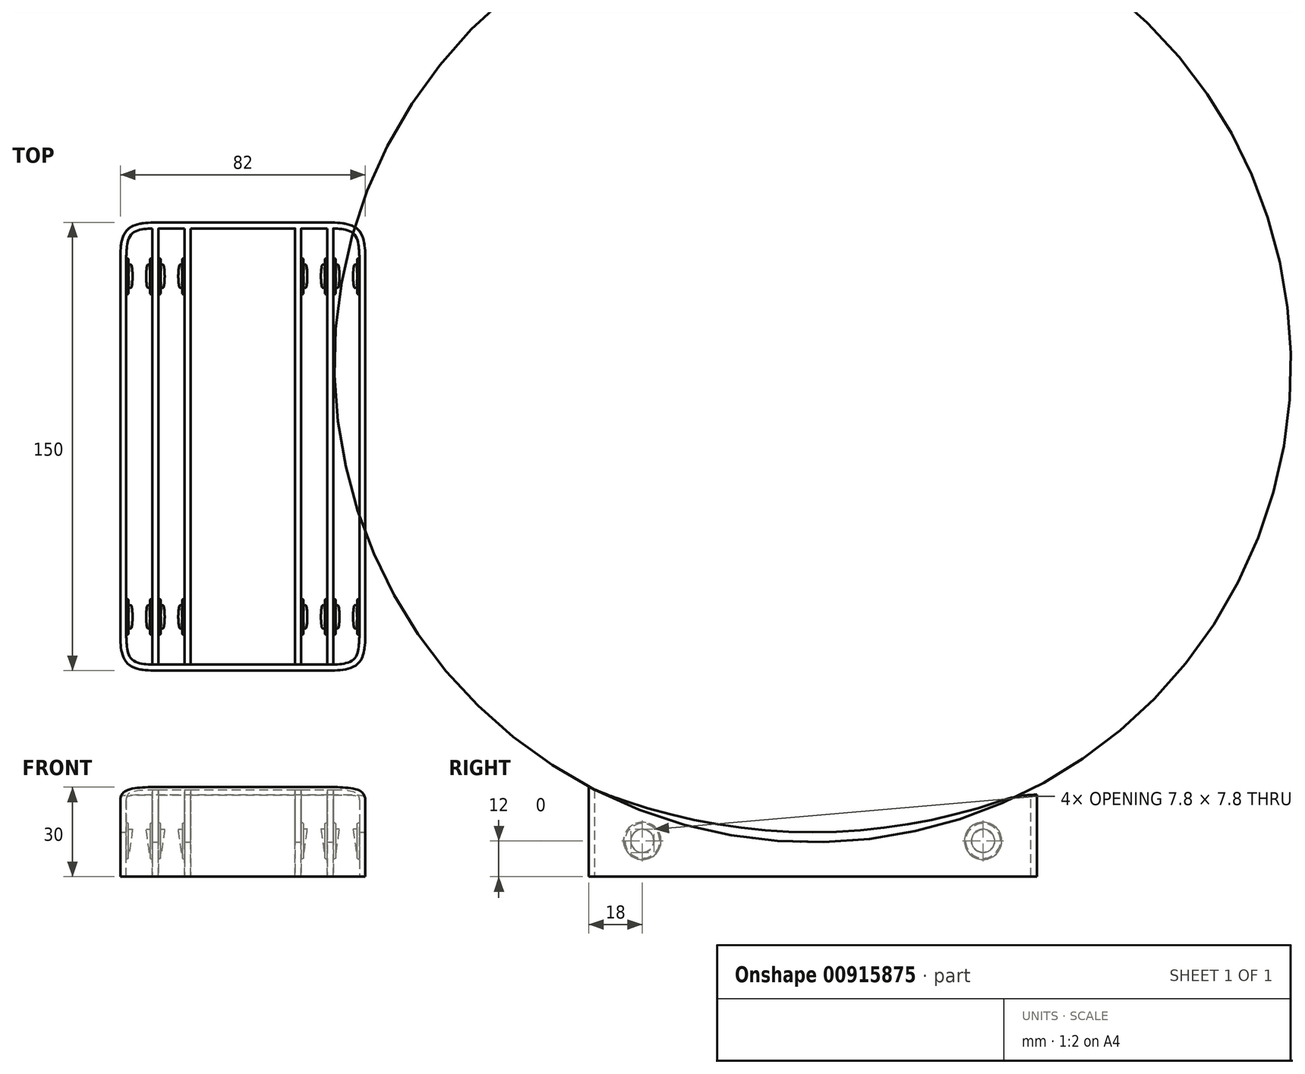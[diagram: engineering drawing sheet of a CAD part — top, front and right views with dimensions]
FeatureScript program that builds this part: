
annotation { "Feature Type Name" : "Feature", "Feature Type Description" : "" }
export const myFeature = defineFeature(function(context is Context, id is Id, definition is map)
    precondition{}
    {
        {
            var Q0;
            Q0=qCreatedBy(makeId("Top.planeOp"),FACE);
            var sketch = newSketch(context, id + "F0", { "sketchPlane" : qUnion([Q0])});
            skLineSegment(sketch, "E0.bottom", {"start": v(-41, 75) * mm, "end": v(41, 75) * mm});
            skLineSegment(sketch, "E0.top", {"start": v(-41, -75) * mm, "end": v(41, -75) * mm});
            skLineSegment(sketch, "E0.left", {"start": v(-41, 75) * mm, "end": v(-41, -75) * mm});
            skLineSegment(sketch, "E0.right", {"start": v(41, 75) * mm, "end": v(41, -75) * mm});
            skPoint(sketch, "E0.middle", {"position": v(0, 0) * mm});
            skSolve(sketch);
        }
        {
            var Q0;
            Q0=qSketchRegion(id+"F0",true);
            extrude(context, id + "F1", {"entities" : qUnion([Q0]), "depth" : 30 * mm, "offsetDistance" : 25 * mm});
        }
        {
            var Q0;
            Q0=makeQuery(id+"F1.opExtrude","SWEPT_EDGE",EDGE,{"disambiguationData":[OSD([sQuery(id+"F0.wireOp",EDGE,"E0.top"),sQuery(id+"F0.wireOp",EDGE,"E0.right")])]});
            var Q1;
            Q1=makeQuery(id+"F1.opExtrude","SWEPT_EDGE",EDGE,{"disambiguationData":[OSD([sQuery(id+"F0.wireOp",EDGE,"E0.top"),sQuery(id+"F0.wireOp",EDGE,"E0.left")])]});
            var Q2;
            Q2=makeQuery(id+"F1.opExtrude","SWEPT_EDGE",EDGE,{"disambiguationData":[OSD([sQuery(id+"F0.wireOp",EDGE,"E0.bottom"),sQuery(id+"F0.wireOp",EDGE,"E0.right")])]});
            var Q3;
            Q3=makeQuery(id+"F1.opExtrude","SWEPT_EDGE",EDGE,{"disambiguationData":[OSD([sQuery(id+"F0.wireOp",EDGE,"E0.bottom"),sQuery(id+"F0.wireOp",EDGE,"E0.left")])]});
            fillet(context, id + "F2", {"entities" : qUnion([Q0, Q1, Q2, Q3]), "radius" : 12 * mm, "tangentPropagation" : true, "rho" : .6, "crossSection" : FilletCrossSection.CONIC, "allowEdgeOverflow" : false});
        }
        {
            var Q0;
            Q0=makeQuery(id+"F20.boolean.opBoolean","COPY",FACE,{"derivedFrom":makeQuery(id+"F20.opExtrude","SWEPT_FACE",FACE,{"disambiguationData":[OSD([sQuery(id+"F19.wireOp",EDGE,"E26")])]})});
            var Q1;
            Q1=makeQuery(id+"F1.opExtrude","CAP_FACE",FACE,{"disambiguationData":[OSD([sQuery(id+"F0.wireOp",EDGE,"E0.bottom"),sQuery(id+"F0.wireOp",EDGE,"E0.top"),sQuery(id+"F0.wireOp",EDGE,"E0.left"),sQuery(id+"F0.wireOp",EDGE,"E0.right")])],"isStart":true});
            var Q2;
            Q2=makeQuery(id+"F1.opExtrude","CAP_FACE",FACE,{"disambiguationData":[OSD([sQuery(id+"F0.wireOp",EDGE,"E0.bottom"),sQuery(id+"F0.wireOp",EDGE,"E0.top"),sQuery(id+"F0.wireOp",EDGE,"E0.left"),sQuery(id+"F0.wireOp",EDGE,"E0.right")])],"isStart":false});
            shell(context, id + "F3", {"entities" : qUnion([Q0, Q1, Q2]), "thickness" : 2 * mm});
        }
        {
            var Q0;
            Q0=makeQuery(id+"F3.opShell","OFFSET_FACE",FACE,{"disambiguationData":[OSD([sQuery(id+"F0.wireOp",EDGE,"E0.bottom")])]});
            cPlane(context, id + "F4", {"entities" : qUnion([Q0]), "cplaneType" : CPlaneType.OFFSET, "offset" : 16 * mm, "width" : 150 * mm, "height" : 150 * mm});
        }
        {
            var Q0;
            Q0=makeQuery(id+"F3.opShell","OFFSET_FACE",FACE,{"disambiguationData":[OSD([sQuery(id+"F0.wireOp",EDGE,"E0.bottom")])]});
            var sketch = newSketch(context, id + "F5", { "sketchPlane" : qUnion([Q0])});
            skLineSegment(sketch, "E1", {"start": v(-30.25, 0) * mm, "end": v(-30.25, 30) * mm});
            skLineSegment(sketch, "E2", {"start": v(-28.25, 30) * mm, "end": v(-30.25, 30) * mm});
            skLineSegment(sketch, "E3", {"start": v(-28.25, 30) * mm, "end": v(-28.25, 0) * mm});
            skLineSegment(sketch, "E4", {"start": v(-28.25, 0) * mm, "end": v(-30.25, 0) * mm});
            skLineSegment(sketch, "E5.bottom", {"start": v(-19.5, 0) * mm, "end": v(-17.5, 0) * mm});
            skLineSegment(sketch, "E5.top", {"start": v(-19.5, 30) * mm, "end": v(-17.5, 30) * mm});
            skLineSegment(sketch, "E5.left", {"start": v(-19.5, 0) * mm, "end": v(-19.5, 30) * mm});
            skLineSegment(sketch, "E5.right", {"start": v(-17.5, 0) * mm, "end": v(-17.5, 30) * mm});
            skLineSegment(sketch, "E6", {"start": v(-19.5, 0) * mm, "end": v(-28.25, 0) * mm, "construction": true});
            skLineSegment(sketch, "E7", {"start": v(-30.25, 0) * mm, "end": v(-39, 0) * mm, "construction": true});
            skSolve(sketch);
        }
        {
            var Q0;
            Q0 = qSketchRegion(id + "F5", true);
            var Q1;
            Q1=makeQuery(id+"F3.opShell","OFFSET_FACE",FACE,{"disambiguationData":[OSD([sQuery(id+"F0.wireOp",EDGE,"E0.top")])]});
            extrude(context, id + "F6", {"entities" : qUnion([Q0]), "operationType" : NewBodyOperationType.ADD, "endBound" : BoundingType.UP_TO_SURFACE, "depth" : 12 * mm, "endBoundEntityFace" : qUnion([Q1]), "offsetDistance" : 25 * mm});
        }
        {
            var Q0;
            Q0=makeQuery(id+"F6.opExtrude","SWEPT_FACE",FACE,{"disambiguationData":[OSD([sQuery(id+"F5.wireOp",EDGE,"E1")])]});
            var sketch = newSketch(context, id + "F7", { "sketchPlane" : qUnion([Q0])});
            skCircle(sketch, "E8", {"center": v(-57, 12) * mm, "radius": 6.25 * mm});
            skSolve(sketch);
        }
        {
            var Q0;
            Q0=qSketchRegion(id+"F7",true);
            var Q1;
            Q1=makeQuery(id+"F6.opExtrude","SWEPT_FACE",FACE,{"disambiguationData":[OSD([sQuery(id+"F5.wireOp",EDGE,"E1")])]});
            extrude(context, id + "F8", {"entities" : qUnion([Q0]), "operationType" : NewBodyOperationType.ADD, "depth" : .75 * mm, "endBoundEntityFace" : qUnion([Q1]), "offsetDistance" : 25 * mm, "hasDraft" : true, "draftAngle" : 30 * degree, "draftPullDirection" : true, "hasSecondDirectionDraft" : true, "secondDirectionDraftAngle" : 15 * degree, "secondDirectionDraftPullDirection" : true});
        }
        {
            var Q0;
            Q0=makeQuery(id+"F3.opShell","OFFSET_FACE",FACE,{"disambiguationData":[OSD([sQuery(id+"F0.wireOp",EDGE,"E0.left")])]});
            var sketch = newSketch(context, id + "F9", { "sketchPlane" : qUnion([Q0])});
            skCircle(sketch, "E9.0", {"center": v(57, 12) * mm, "radius": 6.25 * mm});
            skSolve(sketch);
        }
        {
            var Q0;
            Q0=qSketchRegion(id+"F9",true);
            extrude(context, id + "F10", {"entities" : qUnion([Q0]), "operationType" : NewBodyOperationType.ADD, "depth" : .75 * mm, "offsetDistance" : 25 * mm, "hasDraft" : true, "draftAngle" : 30 * degree, "draftPullDirection" : true});
        }
        {
            var Q0;
            Q0=makeQuery(id+"F6.opExtrude","SWEPT_FACE",FACE,{"disambiguationData":[OSD([sQuery(id+"F5.wireOp",EDGE,"E3")])]});
            var sketch = newSketch(context, id + "F11", { "sketchPlane" : qUnion([Q0])});
            skCircle(sketch, "E10.0", {"center": v(57, 12) * mm, "radius": 6.25 * mm});
            skSolve(sketch);
        }
        {
            var Q0;
            Q0=makeQuery(id+"F6.opExtrude","SWEPT_FACE",FACE,{"disambiguationData":[OSD([sQuery(id+"F5.wireOp",EDGE,"E5.left")])]});
            var sketch = newSketch(context, id + "F12", { "sketchPlane" : qUnion([Q0])});
            skCircle(sketch, "E11.0", {"center": v(-57, 12) * mm, "radius": 6.25 * mm});
            skSolve(sketch);
        }
        {
            var Q0;
            Q0 = qSketchRegion(id + "F11", true);
            extrude(context, id + "F13", {"entities" : qUnion([Q0]), "operationType" : NewBodyOperationType.ADD, "depth" : .75 * mm, "offsetDistance" : 25 * mm, "hasDraft" : true, "draftAngle" : 30 * degree, "draftPullDirection" : true});
        }
        {
            var Q0;
            Q0 = qSketchRegion(id + "F12", true);
            var Q1;
            Q1 = qSketchRegion(id + "F15", true);
            extrude(context, id + "F14", {"entities" : qUnion([Q0, Q1]), "operationType" : NewBodyOperationType.ADD, "depth" : .75 * mm, "offsetDistance" : 25 * mm, "hasDraft" : true, "draftAngle" : 30 * degree, "draftPullDirection" : true});
        }
        {
            var Q0;
            Q0=makeQuery(id+"F8.opExtrude","CAP_FACE",FACE,{"disambiguationData":[OSD([sQuery(id+"F7.wireOp",EDGE,"E8")])],"isStart":false});
            var sketch = newSketch(context, id + "F15", { "sketchPlane" : qUnion([Q0])});
            skCircle(sketch, "E12", {"center": v(-57, 12) * mm, "radius": 3.9 * mm});
            skLineSegment(sketch, "E13", {"start": v(-57, 8.1) * mm, "end": v(-57, 15.9) * mm, "construction": true});
            skSolve(sketch);
        }
        {
            var Q0;
            Q0=qSketchRegion(id+"F15",true);
            var Q1;
            Q1=makeQuery(id+"F10.opExtrude","CAP_FACE",FACE,{"disambiguationData":[OSD([sQuery(id+"F9.wireOp",EDGE,"E9.0")])],"isStart":false});
            var Q2;
            Q2=makeQuery(id+"F14.opExtrude","CAP_FACE",FACE,{"disambiguationData":[OSD([sQuery(id+"F12.wireOp",EDGE,"E11.0")])],"isStart":false});
            extrude(context, id + "F16", {"entities" : qUnion([Q0]), "operationType" : NewBodyOperationType.ADD, "endBound" : BoundingType.UP_TO_SURFACE, "depth" : 25 * mm, "endBoundEntityFace" : qUnion([Q1]), "offsetDistance" : 25 * mm, "hasSecondDirection" : true, "secondDirectionBound" : SecondDirectionBoundingType.UP_TO_SURFACE, "secondDirectionOppositeDirection" : true, "secondDirectionDepth" : 25 * mm, "secondDirectionBoundEntityFace" : qUnion([Q2])});
        }
        {
            var Q0;
            Q0=qCreatedBy(id+"F4.planeOp",FACE);
            var sketch = newSketch(context, id + "F17", { "sketchPlane" : qUnion([Q0])});
            skLineSegment(sketch, "E14", {"start": v(-36.9, 15.9) * mm, "end": v(-38, 8.1) * mm});
            skLineSegment(sketch, "E15", {"start": v(-38, 8.1) * mm, "end": v(-31.25, 8.1) * mm});
            skLineSegment(sketch, "E16", {"start": v(-32.35, 15.9) * mm, "end": v(-31.25, 8.1) * mm});
            skLineSegment(sketch, "E17", {"start": v(-32.35, 15.9) * mm, "end": v(-36.9, 15.9) * mm});
            skLineSegment(sketch, "E18", {"start": v(-31.25, 8.1) * mm, "end": v(-31, 8.1) * mm, "construction": true});
            skLineSegment(sketch, "E19", {"start": v(-38, 8.1) * mm, "end": v(-38.25, 8.1) * mm, "construction": true});
            skLineSegment(sketch, "E20", {"start": v(-27.25, 8.1) * mm, "end": v(-26.15, 15.9) * mm});
            skLineSegment(sketch, "E21", {"start": v(-26.15, 15.9) * mm, "end": v(-21.6, 15.9) * mm});
            skLineSegment(sketch, "E22", {"start": v(-21.6, 15.9) * mm, "end": v(-20.5, 8.1) * mm});
            skLineSegment(sketch, "E23", {"start": v(-20.5, 8.1) * mm, "end": v(-27.25, 8.1) * mm});
            skLineSegment(sketch, "E24", {"start": v(-27.25, 8.1) * mm, "end": v(-27.5, 8.1) * mm, "construction": true});
            skLineSegment(sketch, "E25", {"start": v(-20.5, 8.1) * mm, "end": v(-20.25, 8.1) * mm, "construction": true});
            skSolve(sketch);
        }
        {
            var Q0;
            Q0=qSketchRegion(id+"F17",true);
            var Q1;
            Q1=makeQuery(id+"F3.opShell","OFFSET_FACE",FACE,{"disambiguationData":[OSD([sQuery(id+"F0.wireOp",EDGE,"E0.bottom"),sQuery(id+"F0.wireOp",EDGE,"E0.left")])]});
            extrude(context, id + "F18", {"entities" : qUnion([Q0]), "operationType" : NewBodyOperationType.REMOVE, "endBound" : BoundingType.SYMMETRIC, "oppositeDirection" : true, "depth" : 12 * mm, "endBoundEntityFace" : qUnion([Q1]), "offsetDistance" : 25 * mm});
        }
        {
            var Q0;
            Q0=makeQuery(id+"F1.opExtrude","SWEPT_FACE",FACE,{"disambiguationData":[OSD([sQuery(id+"F0.wireOp",EDGE,"E0.right")])]});
            var sketch = newSketch(context, id + "F19", { "sketchPlane" : qUnion([Q0])});
            skArc(sketch, "E26", {"start": v(-75, 30) * mm, "mid": v(0, 14.92) * mm, "end": v(75, 30) * mm});
            skLineSegment(sketch, "E27", {"start": v(-75, 30) * mm, "end": v(75, 30) * mm});
            skCircle(sketch, "E28", {"center": v(57, 12) * mm, "radius": 11 * mm, "construction": true});
            skArc(sketch, "E29", {"start": v(0, 2.94) * mm, "mid": v(53.33, 23.3) * mm, "end": v(79.5, 74.05) * mm, "construction": true});
            skLineSegment(sketch, "E30", {"start": v(0, 2.94) * mm, "end": v(-29.27, 2.94) * mm, "construction": true});
            skLineSegment(sketch, "E31", {"start": v(-24.7, 7.25) * mm, "end": v(0, 7.25) * mm, "construction": true});
            skPoint(sketch, "E31.endSnap0", {"position": v(0, 14.92) * mm});
            skArc(sketch, "E32", {"start": v(0, 7.25) * mm, "mid": v(58.45, 26.1) * mm, "end": v(94.85, 75.57) * mm, "construction": true});
            skSolve(sketch);
        }
        {
            var Q0;
            Q0=qSketchRegion(id+"F19",true);
            extrude(context, id + "F20", {"entities" : qUnion([Q0]), "operationType" : NewBodyOperationType.REMOVE, "endBound" : BoundingType.THROUGH_ALL, "oppositeDirection" : true, "depth" : 25 * mm, "offsetDistance" : 25 * mm});
        }
        {
            var Q0;
            Q0=qCreatedBy(makeId("Front.planeOp"),FACE);
            var sketch = newSketch(context, id + "F21", { "sketchPlane" : qUnion([Q0])});
            skLineSegment(sketch, "E33", {"start": v(0, 0) * mm, "end": v(0, 24.52) * mm, "construction": true});
            skSolve(sketch);
        }
        {
            var Q0;
            Q0=makeQuery(id+"F1.opExtrude","SWEPT_BODY",BODY,{"disambiguationData":[OSD([sQuery(id+"F0.wireOp",EDGE,"E0.bottom"),sQuery(id+"F0.wireOp",EDGE,"E0.top"),sQuery(id+"F0.wireOp",EDGE,"E0.left"),sQuery(id+"F0.wireOp",EDGE,"E0.right")])]});
            var Q1;
            Q1=sQuery(id+"F21.wireOp",EDGE,"E33");
            circularPattern(context, id + "F22", {"operationType" : NewBodyOperationType.ADD, "entities" : qUnion([Q0]), "axis" : qUnion([Q1]), "angle" : 360 * degree, "instanceCount" : 2, "equalSpace" : true});
        }
        {
            var Q0;
            Q0=makeQuery(id+"F1.opExtrude","SWEPT_BODY",BODY,{"disambiguationData":[OSD([sQuery(id+"F0.wireOp",EDGE,"E0.bottom"),sQuery(id+"F0.wireOp",EDGE,"E0.top"),sQuery(id+"F0.wireOp",EDGE,"E0.left"),sQuery(id+"F0.wireOp",EDGE,"E0.right")])]});
            var Q1;
            Q1=qCreatedBy(makeId("Right.planeOp"),FACE);
            mirror(context, id + "F23", {"operationType" : NewBodyOperationType.ADD, "entities" : qUnion([Q0]), "mirrorPlane" : qUnion([Q1])});
        }
        {
            var Q0;
            Q0=qCreatedBy(makeId("Top.planeOp"),FACE);
            var sketch = newSketch(context, id + "F24", { "sketchPlane" : qUnion([Q0])});
            skLineSegment(sketch, "E34.bottom", {"start": v(38.22, 88.74) * mm, "end": v(-49.86, 88.74) * mm});
            skLineSegment(sketch, "E34.top", {"start": v(38.22, 39.81) * mm, "end": v(-49.86, 39.81) * mm});
            skLineSegment(sketch, "E34.left", {"start": v(38.22, 88.74) * mm, "end": v(38.22, 39.81) * mm});
            skLineSegment(sketch, "E34.right", {"start": v(-49.86, 88.74) * mm, "end": v(-49.86, 39.81) * mm});
            skPoint(sketch, "E34.middle", {"position": v(-5.82, 64.28) * mm});
            skSolve(sketch);
        }
        {
            var Q0;
            Q0=makeQuery(id+"F22.opPattern","COPY",FACE,{"derivedFrom":makeQuery(id+"F6.opExtrude","SWEPT_FACE",FACE,{"disambiguationData":[OSD([sQuery(id+"F5.wireOp",EDGE,"E1")])]}),"instanceName":"1"});
            var sketch = newSketch(context, id + "F25", { "sketchPlane" : qUnion([Q0])});
            skLineSegment(sketch, "E35", {"start": v(72.98, 29.17) * mm, "end": v(-72.98, 29.17) * mm});
            skArc(sketch, "E36", {"start": v(-72.98, 29.17) * mm, "mid": v(0, 11.55) * mm, "end": v(72.98, 29.17) * mm});
            skSolve(sketch);
        }
        {
            var Q0;
            Q0=qSketchRegion(id+"F25",true);
            var Q1;
            Q1=makeQuery(id+"F6.opExtrude","SWEPT_FACE",FACE,{"disambiguationData":[OSD([sQuery(id+"F5.wireOp",EDGE,"E1")])]});
            extrude(context, id + "F26", {"entities" : qUnion([Q0]), "operationType" : NewBodyOperationType.REMOVE, "endBound" : BoundingType.UP_TO_SURFACE, "oppositeDirection" : true, "depth" : 25 * mm, "endBoundEntityFace" : qUnion([Q1]), "offsetDistance" : 25 * mm});
        }
        {
            var Q0;
            Q0=makeQuery(id+"F1.opExtrude","SWEPT_FACE",FACE,{"disambiguationData":[OSD([sQuery(id+"F0.wireOp",EDGE,"E0.right")])]});
            var sketch = newSketch(context, id + "F27", { "sketchPlane" : qUnion([Q0])});
            skArc(sketch, "E37", {"start": v(75, 27.43) * mm, "mid": v(68.92, 26.93) * mm, "end": v(63, 25.43) * mm});
            skLineSegment(sketch, "E38", {"start": v(75, 27.43) * mm, "end": v(76.34, 27.43) * mm, "construction": true});
            skLineSegment(sketch, "E39", {"start": v(75, 30) * mm, "end": v(63, 25.43) * mm});
            skLineSegment(sketch, "E40", {"start": v(75, 27.43) * mm, "end": v(75, 30) * mm});
            skSolve(sketch);
        }
        {
            var Q0;
            Q0=makeQuery(id+"F27.imprint","IMPRINT",FACE,{"disambiguationData":[TD([[makeQuery(id+"F27.imprint","IMPRINT",EDGE,{"derivedFrom":sQuery(id+"F27.wireOp",EDGE,"E37")}),-1.0]])]});
            var Q1;
            Q1=sQuery(id+"F27.wireOp",EDGE,"E38");
            extrude(context, id + "F28", {"entities" : qUnion([Q0]), "operationType" : NewBodyOperationType.REMOVE, "surfaceEntities" : qUnion([Q1]), "endBound" : BoundingType.THROUGH_ALL, "oppositeDirection" : true, "depth" : 25 * mm, "offsetDistance" : 25 * mm});
        }
        {
            var Q0;
            Q0=makeQuery(id+"F28.boolean.opBoolean","INTERSECT",EDGE,{"derivedFrom":[makeQuery(id+"F26.boolean.opBoolean","COPY",FACE,{"disambiguationData":[TD([makeQuery(id+"F22.opPattern","COPY",FACE,{"derivedFrom":makeQuery(id+"F6.opExtrude","SWEPT_FACE",FACE,{"disambiguationData":[OSD([sQuery(id+"F5.wireOp",EDGE,"E1")])]}),"instanceName":"1"})])],"derivedFrom":makeQuery(id+"F26.opExtrude","SWEPT_FACE",FACE,{"disambiguationData":[OSD([sQuery(id+"F25.wireOp",EDGE,"E36")])]})}),makeQuery(id+"F28.opExtrude","SWEPT_FACE",FACE,{"disambiguationData":[OSD([sQuery(id+"F27.wireOp",EDGE,"E37")])]})]});
            var Q1;
            Q1=makeQuery(id+"F28.boolean.opBoolean","INTERSECT",EDGE,{"derivedFrom":[makeQuery(id+"F26.boolean.opBoolean","COPY",FACE,{"disambiguationData":[TD([makeQuery(id+"F22.opPattern","COPY",FACE,{"derivedFrom":makeQuery(id+"F6.opExtrude","SWEPT_FACE",FACE,{"disambiguationData":[OSD([sQuery(id+"F5.wireOp",EDGE,"E5.right")])]}),"instanceName":"1"})])],"derivedFrom":makeQuery(id+"F26.opExtrude","SWEPT_FACE",FACE,{"disambiguationData":[OSD([sQuery(id+"F25.wireOp",EDGE,"E36")])]})}),makeQuery(id+"F28.opExtrude","SWEPT_FACE",FACE,{"disambiguationData":[OSD([sQuery(id+"F27.wireOp",EDGE,"E37")])]})]});
            var Q2;
            Q2=makeQuery(id+"F28.boolean.opBoolean","INTERSECT",EDGE,{"derivedFrom":[makeQuery(id+"F26.boolean.opBoolean","COPY",FACE,{"disambiguationData":[TD([makeQuery(id+"F6.opExtrude","SWEPT_FACE",FACE,{"disambiguationData":[OSD([sQuery(id+"F5.wireOp",EDGE,"E5.left")])]})])],"derivedFrom":makeQuery(id+"F26.opExtrude","SWEPT_FACE",FACE,{"disambiguationData":[OSD([sQuery(id+"F25.wireOp",EDGE,"E36")])]})}),makeQuery(id+"F28.opExtrude","SWEPT_FACE",FACE,{"disambiguationData":[OSD([sQuery(id+"F27.wireOp",EDGE,"E37")])]})]});
            var Q3;
            Q3=makeQuery(id+"F28.boolean.opBoolean","INTERSECT",EDGE,{"derivedFrom":[makeQuery(id+"F26.boolean.opBoolean","COPY",FACE,{"disambiguationData":[TD([makeQuery(id+"F6.opExtrude","SWEPT_FACE",FACE,{"disambiguationData":[OSD([sQuery(id+"F5.wireOp",EDGE,"E1")])]})])],"derivedFrom":makeQuery(id+"F26.opExtrude","SWEPT_FACE",FACE,{"disambiguationData":[OSD([sQuery(id+"F25.wireOp",EDGE,"E36")])]})}),makeQuery(id+"F28.opExtrude","SWEPT_FACE",FACE,{"disambiguationData":[OSD([sQuery(id+"F27.wireOp",EDGE,"E37")])]})]});
            fillet(context, id + "F29", {"entities" : qUnion([Q0, Q1, Q2, Q3]), "tangentPropagation" : true, "radius" : 21 * mm, "defaultsChanged" : true, "vertexSettings" : [], "allowEdgeOverflow" : false});
        }
    });
